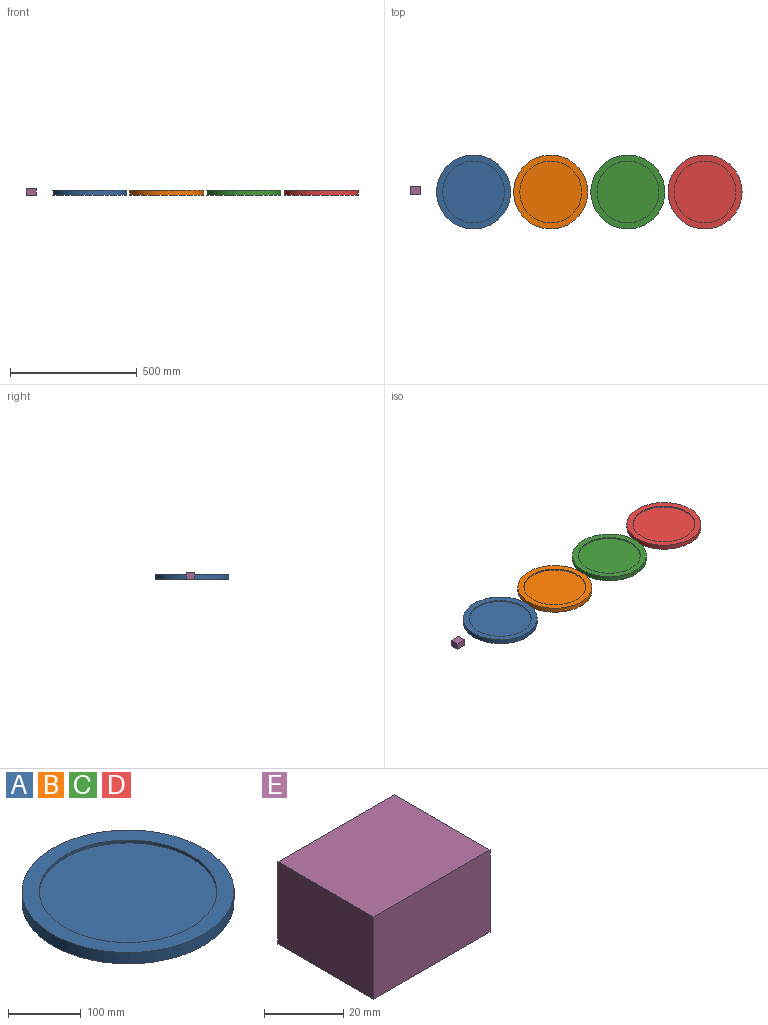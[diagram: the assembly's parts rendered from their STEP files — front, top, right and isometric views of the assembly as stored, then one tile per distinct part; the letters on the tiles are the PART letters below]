
ASSEMBLY  parts=5 mates=1
PART A: 5 faces, bbox 292.1x292.1x19.1 mm
  f0: cylinder r=146.05mm len=292.1mm, axis (0,0,-1), area 17481.4mm2, adj f1,f2
  f1: plane 292.1x292.1mm, normal (0,0,1), area 20070.4mm2, adj f0,f3
  f2: plane 292.1x292.1mm, normal (0,0,-1), area 67012.1mm2, adj f0
  f3: cylinder r=122.24mm len=244.48mm, axis (0,0,1), area 3657.8mm2, adj f1,f4
  f4: plane 244.48x244.48mm, normal (0,0,1), area 46941.7mm2, adj f3
PART B: same geometry as A
PART C: same geometry as A
PART D: same geometry as A
PART E: 6 faces, bbox 41.5x34.2x25.4 mm
  f0: plane 34.17x25.4mm, normal (-1,0,0), area 867.9mm2, adj f1,f3,f4,f5
  f1: plane 41.48x25.4mm, normal (0,-1,0), area 1053.5mm2, adj f0,f2,f4,f5
  f2: plane 34.17x25.4mm, normal (1,0,0), area 867.9mm2, adj f1,f3,f4,f5
  f3: plane 41.48x25.4mm, normal (0,1,0), area 1053.5mm2, adj f0,f2,f4,f5
  f4: plane 41.48x34.17mm, normal (0,0,1), area 1417.2mm2, adj f0,f1,f2,f3
  f5: plane 41.48x34.17mm, normal (0,0,-1), area 1417.2mm2, adj f0,f1,f2,f3
PLACE A t=(-146.05,-146.05,0)mm
PLACE B t=(158.75,-146.05,0)mm
PLACE C t=(463.55,-146.05,0)mm
PLACE D t=(768.35,-146.05,0)mm
PLACE E t=(-251.28,-10.71,0)mm
MATE planar E.f5 <-> A.f0  axis (0,0,-1) through (-230.54,6.37,0)mm
